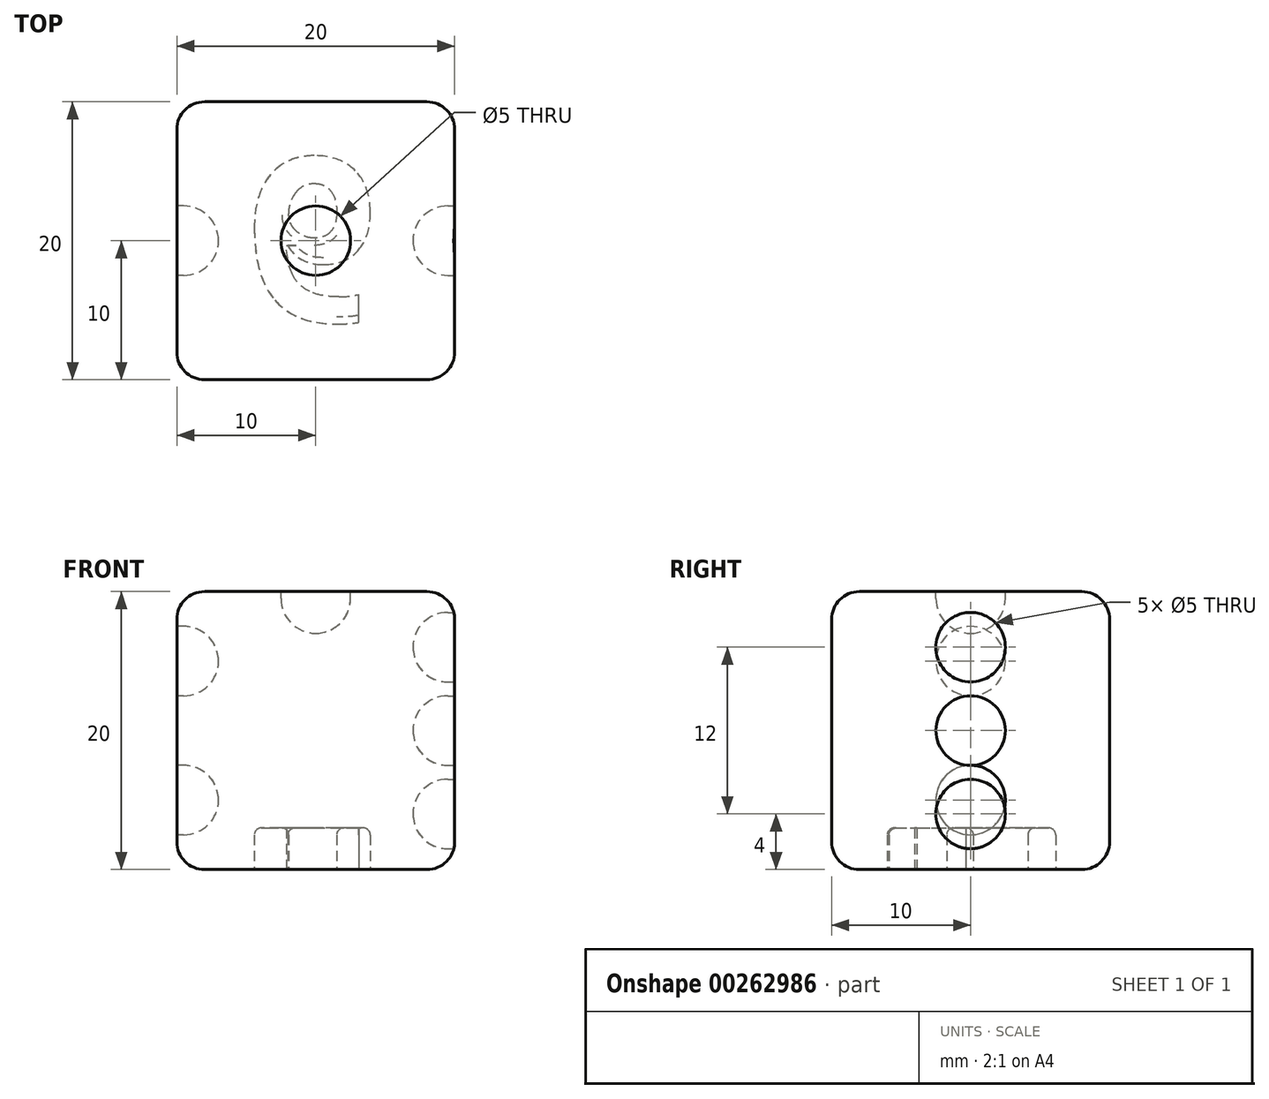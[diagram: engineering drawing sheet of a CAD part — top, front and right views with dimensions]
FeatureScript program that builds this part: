
annotation { "Feature Type Name" : "Feature", "Feature Type Description" : "" }
export const myFeature = defineFeature(function(context is Context, id is Id, definition is map)
    precondition{}
    {
        {
            var Q0;
            Q0=qCreatedBy(makeId("Top.planeOp"),FACE);
            var sketch = newSketch(context, id + "F0", { "sketchPlane" : qUnion([Q0])});
            skLineSegment(sketch, "E0.bottom", {"start": v(0, 0) * mm, "end": v(20, 0) * mm});
            skLineSegment(sketch, "E0.top", {"start": v(0, 20) * mm, "end": v(20, 20) * mm});
            skLineSegment(sketch, "E0.left", {"start": v(0, 0) * mm, "end": v(0, 20) * mm});
            skLineSegment(sketch, "E0.right", {"start": v(20, 0) * mm, "end": v(20, 20) * mm});
            skSolve(sketch);
        }
        {
            var Q0;
            Q0=makeQuery(id+"F0.imprint","IMPRINT",FACE,{"disambiguationData":[TD([[makeQuery(id+"F0.imprint","IMPRINT",EDGE,{"derivedFrom":sQuery(id+"F0.wireOp",EDGE,"E0.bottom")}),1.0]])]});
            extrude(context, id + "F1", {"entities" : qUnion([Q0]), "depth" : 20 * mm});
        }
        {
            var Q0;
            Q0=makeQuery(id+"F1.opExtrude","CAP_FACE",FACE,{"disambiguationData":[OSD([sQuery(id+"F0.wireOp",EDGE,"E0.bottom"),sQuery(id+"F0.wireOp",EDGE,"E0.top"),sQuery(id+"F0.wireOp",EDGE,"E0.left"),sQuery(id+"F0.wireOp",EDGE,"E0.right")])],"isStart":false});
            var sketch = newSketch(context, id + "F2", { "sketchPlane" : qUnion([Q0])});
            skCircle(sketch, "E1", {"center": v(10, 10) * mm, "radius": 2.5 * mm});
            skSolve(sketch);
        }
        {
            var Q0;
            Q0=makeQuery(id+"F2.imprint","IMPRINT",FACE,{"disambiguationData":[TD([[makeQuery(id+"F2.imprint","IMPRINT",EDGE,{"derivedFrom":sQuery(id+"F2.wireOp",EDGE,"E1")}),1.0]])]});
            extrude(context, id + "F3", {"entities" : qUnion([Q0]), "operationType" : NewBodyOperationType.REMOVE, "oppositeDirection" : true, "depth" : 3 * mm});
        }
        {
            var Q0;
            Q0=makeQuery(id+"F3.boolean.opBoolean","COPY",EDGE,{"derivedFrom":makeQuery(id+"F3.opExtrude","CAP_EDGE",EDGE,{"disambiguationData":[OSD([sQuery(id+"F2.wireOp",EDGE,"E1")])],"isStart":false})});
            fillet(context, id + "F4", {"entities" : qUnion([Q0]), "radius" : 2.5 * mm, "tangentPropagation" : true, "allowEdgeOverflow" : false});
        }
        {
            var Q0;
            Q0=makeQuery(id+"F1.opExtrude","CAP_EDGE",EDGE,{"disambiguationData":[OSD([sQuery(id+"F0.wireOp",EDGE,"E0.right")])],"isStart":false});
            var Q1;
            Q1=makeQuery(id+"F1.opExtrude","CAP_EDGE",EDGE,{"disambiguationData":[OSD([sQuery(id+"F0.wireOp",EDGE,"E0.left")])],"isStart":false});
            var Q2;
            Q2=makeQuery(id+"F1.opExtrude","CAP_EDGE",EDGE,{"disambiguationData":[OSD([sQuery(id+"F0.wireOp",EDGE,"E0.bottom")])],"isStart":false});
            var Q3;
            Q3=makeQuery(id+"F1.opExtrude","SWEPT_EDGE",EDGE,{"disambiguationData":[OSD([sQuery(id+"F0.wireOp",EDGE,"E0.bottom"),sQuery(id+"F0.wireOp",EDGE,"E0.left")])]});
            var Q4;
            Q4=makeQuery(id+"F1.opExtrude","SWEPT_EDGE",EDGE,{"disambiguationData":[OSD([sQuery(id+"F0.wireOp",EDGE,"E0.top"),sQuery(id+"F0.wireOp",EDGE,"E0.left")])]});
            var Q5;
            Q5=makeQuery(id+"F1.opExtrude","CAP_EDGE",EDGE,{"disambiguationData":[OSD([sQuery(id+"F0.wireOp",EDGE,"E0.top")])],"isStart":false});
            var Q6;
            Q6=makeQuery(id+"F1.opExtrude","SWEPT_EDGE",EDGE,{"disambiguationData":[OSD([sQuery(id+"F0.wireOp",EDGE,"E0.bottom"),sQuery(id+"F0.wireOp",EDGE,"E0.right")])]});
            var Q7;
            Q7=makeQuery(id+"F1.opExtrude","SWEPT_EDGE",EDGE,{"disambiguationData":[OSD([sQuery(id+"F0.wireOp",EDGE,"E0.top"),sQuery(id+"F0.wireOp",EDGE,"E0.right")])]});
            var Q8;
            Q8=makeQuery(id+"F1.opExtrude","CAP_EDGE",EDGE,{"disambiguationData":[OSD([sQuery(id+"F0.wireOp",EDGE,"E0.right")])],"isStart":true});
            var Q9;
            Q9=makeQuery(id+"F1.opExtrude","CAP_EDGE",EDGE,{"disambiguationData":[OSD([sQuery(id+"F0.wireOp",EDGE,"E0.top")])],"isStart":true});
            var Q10;
            Q10=makeQuery(id+"F1.opExtrude","CAP_EDGE",EDGE,{"disambiguationData":[OSD([sQuery(id+"F0.wireOp",EDGE,"E0.bottom")])],"isStart":true});
            var Q11;
            Q11=makeQuery(id+"F1.opExtrude","CAP_EDGE",EDGE,{"disambiguationData":[OSD([sQuery(id+"F0.wireOp",EDGE,"E0.left")])],"isStart":true});
            fillet(context, id + "F5", {"entities" : qUnion([Q0, Q1, Q2, Q3, Q4, Q5, Q6, Q7, Q8, Q9, Q10, Q11]), "radius" : 2 * mm, "tangentPropagation" : true, "allowEdgeOverflow" : false});
        }
        {
            var Q0;
            Q0=makeQuery(id+"F1.opExtrude","SWEPT_FACE",FACE,{"disambiguationData":[OSD([sQuery(id+"F0.wireOp",EDGE,"E0.left")])]});
            var sketch = newSketch(context, id + "F6", { "sketchPlane" : qUnion([Q0])});
            skCircle(sketch, "E2", {"center": v(-10, 15) * mm, "radius": 2.5 * mm});
            skCircle(sketch, "E3", {"center": v(-10, 5) * mm, "radius": 2.5 * mm});
            skSolve(sketch);
        }
        {
            var Q0;
            Q0=makeQuery(id+"F6.imprint","IMPRINT",FACE,{"disambiguationData":[TD([[makeQuery(id+"F6.imprint","IMPRINT",EDGE,{"derivedFrom":sQuery(id+"F6.wireOp",EDGE,"E2")}),1.0]])]});
            var Q1;
            Q1=makeQuery(id+"F6.imprint","IMPRINT",FACE,{"disambiguationData":[TD([[makeQuery(id+"F6.imprint","IMPRINT",EDGE,{"derivedFrom":sQuery(id+"F6.wireOp",EDGE,"E3")}),1.0]])]});
            extrude(context, id + "F7", {"entities" : qUnion([Q0, Q1]), "operationType" : NewBodyOperationType.REMOVE, "oppositeDirection" : true, "depth" : 3 * mm});
        }
        {
            var Q0;
            Q0=makeQuery(id+"F7.boolean.opBoolean","COPY",EDGE,{"derivedFrom":makeQuery(id+"F7.opExtrude","CAP_EDGE",EDGE,{"disambiguationData":[OSD([sQuery(id+"F6.wireOp",EDGE,"E2")])],"isStart":false})});
            var Q1;
            Q1=makeQuery(id+"F7.boolean.opBoolean","COPY",EDGE,{"derivedFrom":makeQuery(id+"F7.opExtrude","CAP_EDGE",EDGE,{"disambiguationData":[OSD([sQuery(id+"F6.wireOp",EDGE,"E3")])],"isStart":false})});
            fillet(context, id + "F8", {"entities" : qUnion([Q0, Q1]), "radius" : 2.5 * mm, "tangentPropagation" : true, "allowEdgeOverflow" : false});
        }
        {
            var Q0;
            Q0=makeQuery(id+"F1.opExtrude","SWEPT_FACE",FACE,{"disambiguationData":[OSD([sQuery(id+"F0.wireOp",EDGE,"E0.right")])]});
            var sketch = newSketch(context, id + "F9", { "sketchPlane" : qUnion([Q0])});
            skCircle(sketch, "E4", {"center": v(10, 16) * mm, "radius": 2.5 * mm});
            skCircle(sketch, "E5", {"center": v(10, 10) * mm, "radius": 2.5 * mm});
            skCircle(sketch, "E6", {"center": v(10, 4) * mm, "radius": 2.5 * mm});
            skSolve(sketch);
        }
        {
            var Q0;
            Q0=makeQuery(id+"F9.imprint","IMPRINT",FACE,{"disambiguationData":[TD([[makeQuery(id+"F9.imprint","IMPRINT",EDGE,{"derivedFrom":sQuery(id+"F9.wireOp",EDGE,"E4")}),1.0]])]});
            var Q1;
            Q1=makeQuery(id+"F9.imprint","IMPRINT",FACE,{"disambiguationData":[TD([[makeQuery(id+"F9.imprint","IMPRINT",EDGE,{"derivedFrom":sQuery(id+"F9.wireOp",EDGE,"E5")}),1.0]])]});
            var Q2;
            Q2=makeQuery(id+"F9.imprint","IMPRINT",FACE,{"disambiguationData":[TD([[makeQuery(id+"F9.imprint","IMPRINT",EDGE,{"derivedFrom":sQuery(id+"F9.wireOp",EDGE,"E6")}),1.0]])]});
            extrude(context, id + "F10", {"entities" : qUnion([Q0, Q1, Q2]), "operationType" : NewBodyOperationType.REMOVE, "oppositeDirection" : true, "depth" : 3 * mm});
        }
        {
            var Q0;
            Q0=makeQuery(id+"F10.boolean.opBoolean","COPY",EDGE,{"derivedFrom":makeQuery(id+"F10.opExtrude","CAP_EDGE",EDGE,{"disambiguationData":[OSD([sQuery(id+"F9.wireOp",EDGE,"E4")])],"isStart":false})});
            var Q1;
            Q1=makeQuery(id+"F10.boolean.opBoolean","COPY",EDGE,{"derivedFrom":makeQuery(id+"F10.opExtrude","CAP_EDGE",EDGE,{"disambiguationData":[OSD([sQuery(id+"F9.wireOp",EDGE,"E5")])],"isStart":false})});
            var Q2;
            Q2=makeQuery(id+"F10.boolean.opBoolean","COPY",EDGE,{"derivedFrom":makeQuery(id+"F10.opExtrude","CAP_EDGE",EDGE,{"disambiguationData":[OSD([sQuery(id+"F9.wireOp",EDGE,"E6")])],"isStart":false})});
            fillet(context, id + "F11", {"entities" : qUnion([Q0, Q1, Q2]), "radius" : 2.5 * mm, "tangentPropagation" : true, "allowEdgeOverflow" : false});
        }
        {
            var Q0;
            Q0=makeQuery(id+"F1.opExtrude","CAP_FACE",FACE,{"disambiguationData":[OSD([sQuery(id+"F0.wireOp",EDGE,"E0.bottom"),sQuery(id+"F0.wireOp",EDGE,"E0.top"),sQuery(id+"F0.wireOp",EDGE,"E0.left"),sQuery(id+"F0.wireOp",EDGE,"E0.right")])],"isStart":true});
            var sketch = newSketch(context, id + "F12", { "sketchPlane" : qUnion([Q0])});
            skText(sketch, "E7", { "text": "6", "fontName": "OpenSans-Bold.ttf"});
            skLineSegment(sketch, "E8", {"start": v(0, -10) * mm, "end": v(5, -10) * mm, "construction": true});
            skPoint(sketch, "E9", {"position": v(18, -10) * mm});
            const initialGuessF12  = {"E7": [0.005, -0.01596, 1, 0, 0.01192]};
            skSetInitialGuess(sketch, initialGuessF12);
            skSolve(sketch);
        }
        {
            var Q0;
            Q0=makeQuery(id+"F12.imprint","IMPRINT",FACE,{"disambiguationData":[TD([[makeQuery(id+"F12.imprint","IMPRINT",EDGE,{"derivedFrom":sQuery(id+"F12.wireOp",EDGE,"E7.sketch_text.stroke-0")}),-1.0]])]});
            extrude(context, id + "F13", {"entities" : qUnion([Q0]), "operationType" : NewBodyOperationType.REMOVE, "oppositeDirection" : true, "depth" : 3 * mm});
        }
        {
            var Q0;
            Q0=makeQuery(id+"F13.boolean.opBoolean","COPY",EDGE,{"derivedFrom":makeQuery(id+"F13.opExtrude","CAP_EDGE",EDGE,{"disambiguationData":[OSD([sQuery(id+"F12.wireOp",EDGE,"E7.sketch_text.stroke-1")])],"isStart":false})});
            var Q1;
            Q1=makeQuery(id+"F13.boolean.opBoolean","COPY",EDGE,{"derivedFrom":makeQuery(id+"F13.opExtrude","CAP_EDGE",EDGE,{"disambiguationData":[OSD([sQuery(id+"F12.wireOp",EDGE,"E7.sketch_text.stroke-23")])],"isStart":false})});
            fillet(context, id + "F14", {"entities" : qUnion([Q0, Q1]), "radius" : .5 * mm, "tangentPropagation" : true, "allowEdgeOverflow" : false});
        }
    });
